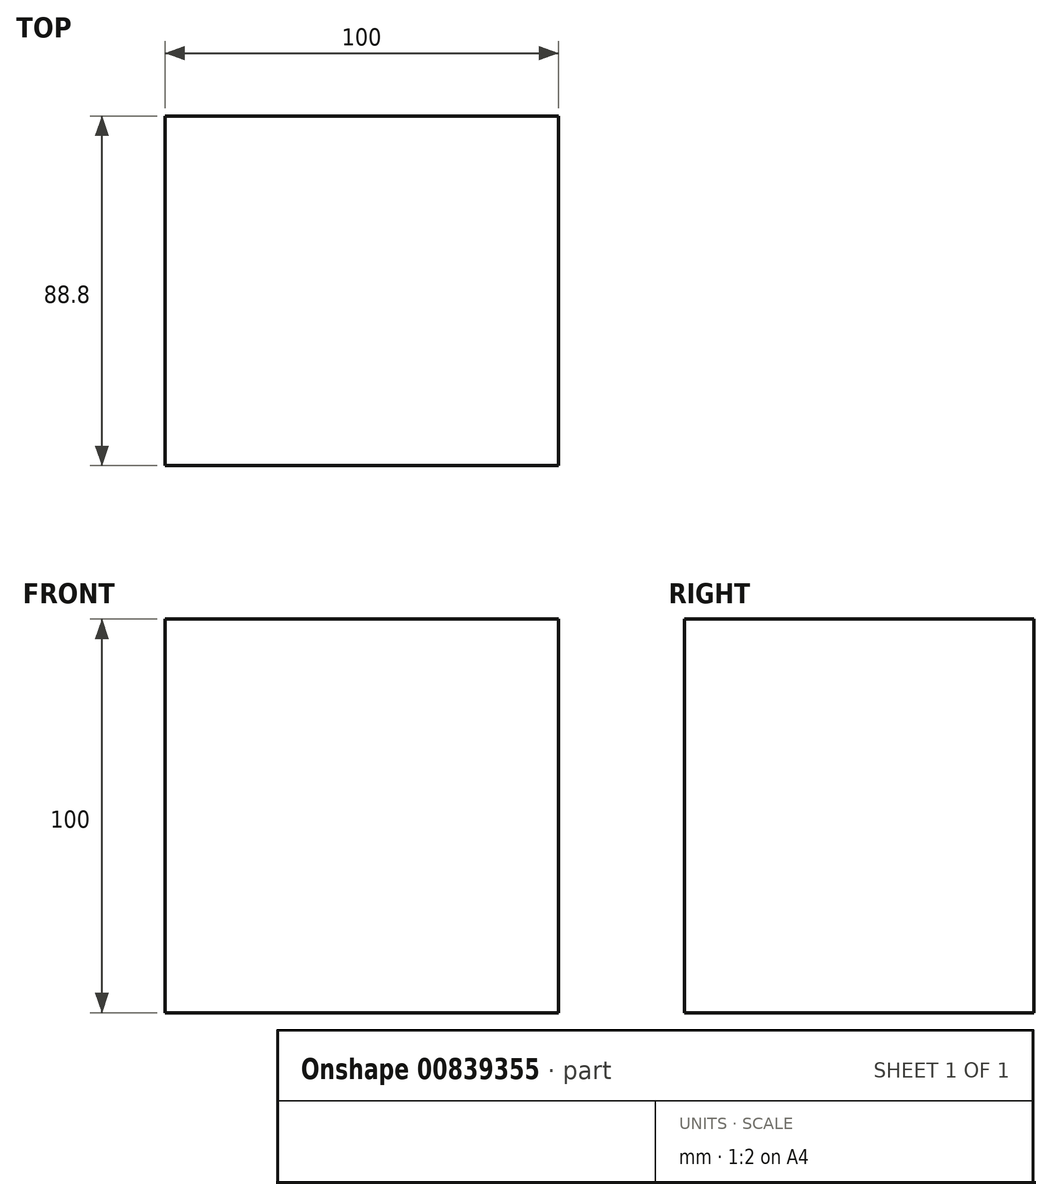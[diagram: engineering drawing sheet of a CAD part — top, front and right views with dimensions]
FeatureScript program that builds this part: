
annotation { "Feature Type Name" : "Feature", "Feature Type Description" : "" }
export const myFeature = defineFeature(function(context is Context, id is Id, definition is map)
    precondition{}
    {
        {
            var Q0;
            Q0=qCreatedBy(makeId("Top.planeOp"),FACE);
            var sketch = newSketch(context, id + "F0", { "sketchPlane" : qUnion([Q0])});
            skLineSegment(sketch, "E0.bottom", {"start": v(-50, 44.4) * mm, "end": v(50, 44.4) * mm});
            skLineSegment(sketch, "E0.top", {"start": v(-50, -44.4) * mm, "end": v(50, -44.4) * mm});
            skLineSegment(sketch, "E0.left", {"start": v(-50, 44.4) * mm, "end": v(-50, -44.4) * mm});
            skLineSegment(sketch, "E0.right", {"start": v(50, 44.4) * mm, "end": v(50, -44.4) * mm});
            skPoint(sketch, "E0.middle", {"position": v(0, 0) * mm});
            skSolve(sketch);
        }
        {
            var Q0;
            Q0 = qSketchRegion(id + "F0", true);
            extrude(context, id + "F1", {"entities" : qUnion([Q0]), "depth" : 100 * mm, "offsetDistance" : 25 * mm});
        }
    });
